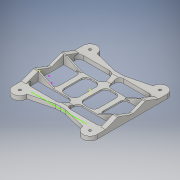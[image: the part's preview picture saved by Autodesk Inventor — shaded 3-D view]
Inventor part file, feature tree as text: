
AUTODESK INVENTOR PART (.ipt)
format: ipt  version: 2016 (Build 200138000, 138)  size: 679,936 bytes
history: native  units: in
note: dims shown in document units (in); Inventor stores cm internally (conversion verified against a paired STEP export)
features: sketch x39, extrude x31, chamfer x11, mirror x6, fillet x3
ambient origin geometry x8: Origin, YZ Plane, XZ Plane, XY Plane, X Axis, Y Axis, Z Axis, Center Point
bodies: Solid1 (feature_tree)
feature tree (90):
  sketch  "Sketch1"  dims[d0=4.5in d1=4.5in]
  extrude  "Extrusion1"  Depth=4.5in
  extrude  "Extrusion2"  Depth=4.2in
  extrude  "Extrusion3"  Depth=1.4in TaperAngle=0.0deg
  extrude  "Extrusion4"  Depth=0.65in
  chamfer  "Chamfer1"  Distance=3.3125in
  extrude  "Extrusion5"  Depth=0.1in TaperAngle=0.0deg
  extrude  "Extrusion6"  Depth=0.75in
  extrude  "Extrusion7"  Depth=2.375in
  extrude  "Extrusion8"  Depth=2.375in
  mirror  "Mirror1"
  mirror  "Mirror2"
  extrude  "Extrusion9"  Depth=2.375in
  mirror  "Mirror3"
  extrude  "Extrusion10"  Depth=3.0375in TaperAngle=0.0deg
  extrude  "Extrusion11"  Depth=1.75in TaperAngle=0.0deg
  extrude  "Extrusion12"  Depth=0.25in
  extrude  "Extrusion13"  Depth=0.25in TaperAngle=0.0deg
  extrude  "Extrusion14"  Depth=1.625in TaperAngle=0.0deg
  extrude  "Extrusion15"  Depth=0.075in TaperAngle=0.0deg
  fillet  "Fillet2"  Radius=0.25in
  fillet  "Fillet3"  Radius=0.25in
  fillet  "Fillet4"  Radius=0.075in
  extrude  "Extrusion16"  Depth=0.25in
  extrude  "Extrusion17"  Depth=0.25in TaperAngle=0.0deg
  sketch  "Sketch19"  dims[d53=0.75in d54=0.0in d55=0.025in d56=0.0in d57=0.25in d58=0.25in d59=0.075in d60=0.0in]
  extrude  "Extrusion18"  Depth=0.1in
  extrude  "Extrusion19"  Depth=0.1in TaperAngle=0.0deg
  extrude  "Extrusion20"  Depth=0.65in TaperAngle=0.0deg
  chamfer  "Chamfer14"  Distance=0.5in
  chamfer  "Chamfer15"  Distance=0.25in Angle=45.0deg
  chamfer  "Chamfer16"  Distance=0.25in Angle=45.0deg
  chamfer  "Chamfer17"  Distance=0.25in Angle=45.0deg
  chamfer  "Chamfer18"  Distance=0.25in Angle=45.0deg
  chamfer  "Chamfer19"  Distance=0.25in Angle=45.0deg
  chamfer  "Chamfer20"  Distance=0.25in Angle=45.0deg
  chamfer  "Chamfer21"  Distance=0.25in Angle=45.0deg
  extrude  "Extrusion21"  Depth=0.65in
  sketch  "Sketch24"  dims[d99=1.4in d100=0.75in d101=0.0in d108=0.5in d109=0.0in d110=0.25in d111=0.65in d112=45.0deg d113=0.25in d114=0.65in d115=45.0deg d116=0.25in d117=0.65in d118=45.0deg d119=0.25in d120=0.65in d121=45.0deg d122=0.25in d123=0.65in d124=45.0deg d125=0.25in d126=0.65in d127=45.0deg d128=0.25in d129=0.65in d130=45.0deg]
  extrude  "Extrusion22"  Depth=0.25in
  chamfer  "Chamfer26"  Distance=0.125in
  chamfer  "Chamfer27"  Distance=0.15in Angle=45.0deg
  sketch  "Sketch26"  dims[d135=0.25in d136=0.0in d149=2.0in]
  extrude  "Extrusion23"  Depth=0.15in TaperAngle=0.0deg
  extrude  "Extrusion24"  Depth=2.75in TaperAngle=0.0deg
  extrude  "Extrusion25"  Depth=0.1299in
  mirror  "Mirror4"
  extrude  "Extrusion26"  Depth=0.1299in
  sketch  "Sketch31"  dims[d194=0.1299in d195=0.1299in]
  sketch  "Sketch32"  dims[d196=4.4375in d197=0.0in d198=2.1875in d199=0.0in]
  extrude  "Extrusion27"  Depth=2.1875in TaperAngle=0.0deg
  extrude  "Extrusion28"  Depth=0.25in TaperAngle=0.0deg
  extrude  "Extrusion29"  Depth=0.25in TaperAngle=0.0deg
  extrude  "Extrusion30"  [1 undecoded]
  sketch  "Sketch37"
  extrude  "Extrusion31"  [1 undecoded]
  mirror  "Mirror5"
  mirror  "Mirror6"
  sketch  "Sketch39"
  sketch  "Sketch2"  dims[d2=1.0in d3=0.0in d4=4.2in]
  sketch  "Sketch3"  dims[d5=1.4in d6=1.0in d7=0.0in]
  sketch  "Sketch4"  dims[d8=4.0in d9=0.65in]
  sketch  "Sketch5"  dims[d10=0.4in]
  sketch  "Sketch6"  dims[d11=4.0in]
  sketch  "Sketch7"  dims[d12=0.65in]
  sketch  "Sketch8"  dims[d13=0.4in d14=3.3125in d15=0.0in]
  sketch  "Sketch9"  dims[d16=1.55in d17=0.1in d18=0.0in]
  sketch  "Sketch10"  dims[d19=0.125in d20=0.125in d21=45.0deg d22=0.75in]
  sketch  "Sketch11"  dims[d23=0.1374in d24=2.375in]
  sketch  "Sketch12"  dims[d26=0.1374in d27=2.375in]
  sketch  "Sketch13"  dims[d28=2.375in d30=2.375in]
  sketch  "Sketch14"  dims[d31=1.525in d32=0.0in d33=3.0375in d34=0.0in]
  sketch  "Sketch15"  dims[d35=0.75in d36=0.0in d41=1.75in d42=0.0in]
  sketch  "Sketch16"  dims[d43=0.25in d44=0.125in]
  sketch  "Sketch17"  dims[d45=0.25in d46=0.0in d47=0.25in d48=0.0in]
  sketch  "Sketch18"  dims[d49=1.1875in d50=0.0in d51=1.625in d52=0.0in]
  sketch  "Sketch20"  dims[d61=0.25in d62=0.25in]
  sketch  "Sketch21"  dims[d63=0.25in d64=0.75in d65=0.0in]
  sketch  "Sketch22"  dims[d66=0.75in d67=0.0in d71=0.1in]
  sketch  "Sketch23"  dims[d72=0.1in d73=0.1in d74=0.0in]
  sketch  "Sketch25"  dims[d131=0.25in d132=0.65in d133=45.0deg d134=3.0in]
  sketch  "Sketch27"  dims[d150=2.0in d151=0.125in d152=0.0in d153=0.35in d154=0.15in d155=45.0deg]
  sketch  "Sketch28"  dims[d156=0.35in d157=0.15in d158=45.0deg d186=2.0625in d187=0.0in]
  sketch  "Sketch29"  dims[d188=2.0625in d189=0.0in d190=2.75in d191=0.0in]
  sketch  "Sketch30"  dims[d192=0.1299in d193=0.1299in]
  sketch  "Sketch33"  dims[d200=0.25in d201=0.0in d202=0.25in d203=0.0in]
  sketch  "Sketch34"  dims[d204=0.25in d205=0.0in d206=2.0625in d207=0.0in]
  sketch  "Sketch35"
  sketch  "Sketch36"
  sketch  "Sketch38"
note: 2 required parameter values undecoded (feature->parameter linkage not recoverable at this tier; creation-order binding heuristic only, values carry confidence <= 0.55)
